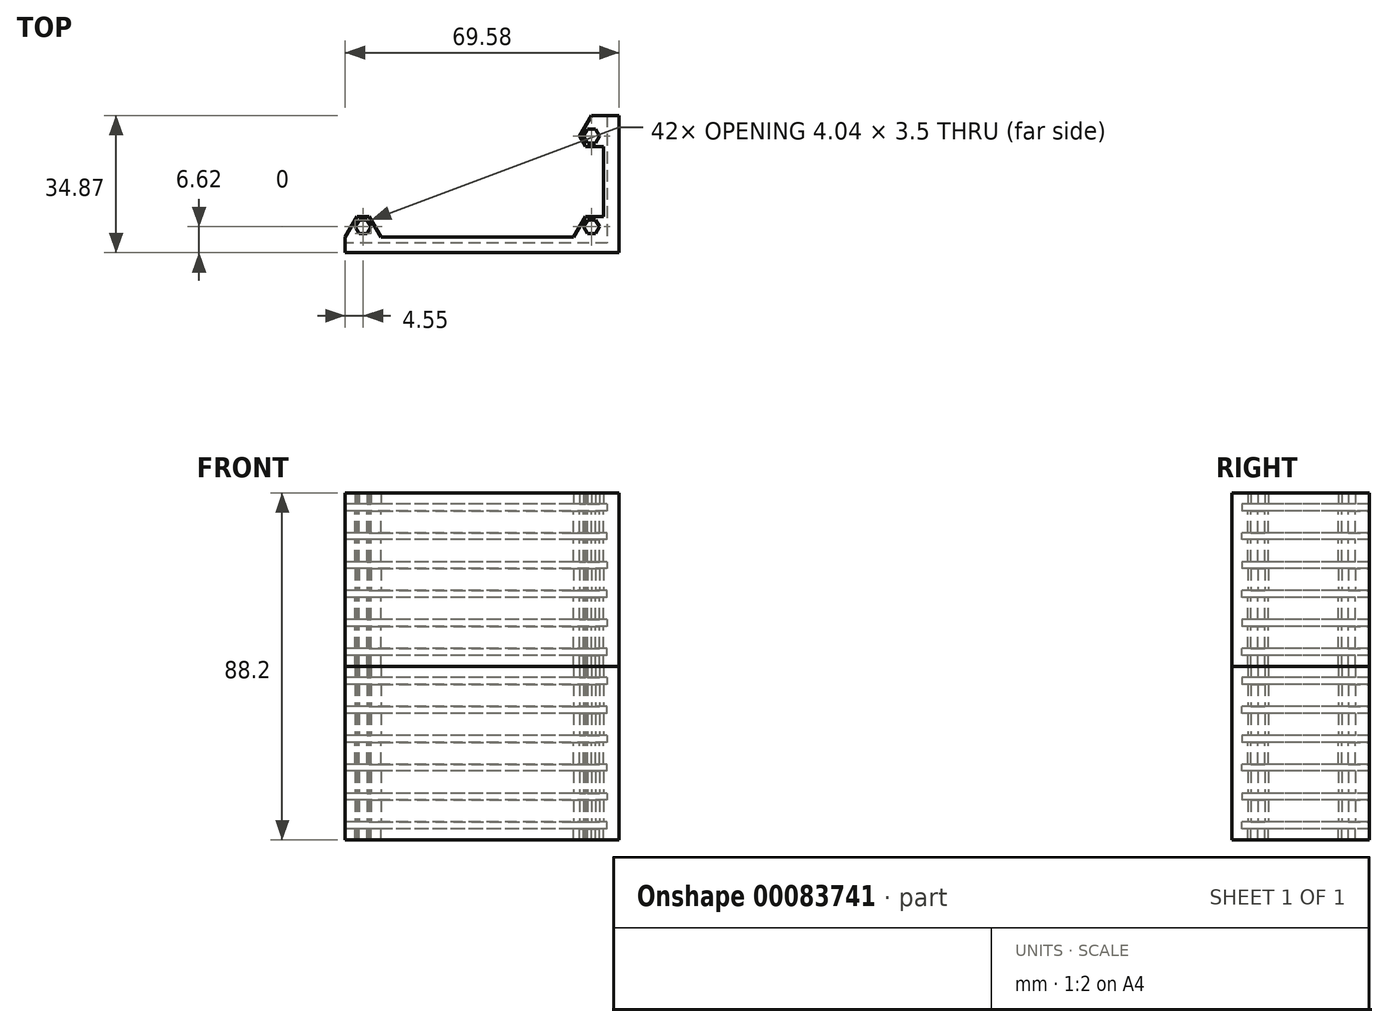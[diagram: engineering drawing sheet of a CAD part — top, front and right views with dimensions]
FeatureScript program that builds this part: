
annotation { "Feature Type Name" : "Feature", "Feature Type Description" : "" }
export const myFeature = defineFeature(function(context is Context, id is Id, definition is map)
    precondition{}
    {
        {
            var Q0;
            Q0=qCreatedBy(makeId("Top.planeOp"),FACE);
            var sketch = newSketch(context, id + "F0", { "sketchPlane" : qUnion([Q0])});
            skLineSegment(sketch, "E0.bottom", {"start": v(-29, 11.5) * mm, "end": v(29, 11.5) * mm, "construction": true});
            skLineSegment(sketch, "E0.top", {"start": v(-29, -11.5) * mm, "end": v(29, -11.5) * mm, "construction": true});
            skLineSegment(sketch, "E0.left", {"start": v(-29, 11.5) * mm, "end": v(-29, -11.5) * mm, "construction": true});
            skLineSegment(sketch, "E0.right", {"start": v(29, 11.5) * mm, "end": v(29, -11.5) * mm, "construction": true});
            skLineSegment(sketch, "E1", {"start": v(0, 11.5) * mm, "end": v(0, -11.5) * mm, "construction": true});
            skCircle(sketch, "E2.cCircle", {"center": v(-29, 11.5) * mm, "radius": 2.62 * mm, "construction": true});
            skLineSegment(sketch, "E2.0", {"start": v(-27.48, 14.12) * mm, "end": v(-25.97, 11.5) * mm});
            skLineSegment(sketch, "E2.1", {"start": v(-25.97, 11.5) * mm, "end": v(-27.48, 8.88) * mm});
            skLineSegment(sketch, "E2.2", {"start": v(-27.48, 8.87) * mm, "end": v(-30.52, 8.87) * mm});
            skLineSegment(sketch, "E2.3", {"start": v(-30.52, 8.88) * mm, "end": v(-32.03, 11.5) * mm});
            skLineSegment(sketch, "E2.4", {"start": v(-32.03, 11.5) * mm, "end": v(-30.52, 14.13) * mm});
            skLineSegment(sketch, "E2.5", {"start": v(-30.52, 14.13) * mm, "end": v(-27.48, 14.13) * mm});
            skLineSegment(sketch, "E3", {"start": v(-29, 0) * mm, "end": v(29, 0) * mm, "construction": true});
            skLineSegment(sketch, "E4.MirrorCS", {"start": v(-27.48, -14.12) * mm, "end": v(-25.97, -11.5) * mm});
            skLineSegment(sketch, "E5.MirrorCS", {"start": v(-25.97, -11.5) * mm, "end": v(-27.48, -8.88) * mm});
            skLineSegment(sketch, "E6.MirrorCS", {"start": v(-27.48, -8.87) * mm, "end": v(-30.52, -8.87) * mm});
            skLineSegment(sketch, "E7.MirrorCS", {"start": v(-30.52, -8.88) * mm, "end": v(-32.03, -11.5) * mm});
            skLineSegment(sketch, "E8.MirrorCS", {"start": v(-30.52, -14.12) * mm, "end": v(-27.48, -14.12) * mm});
            skLineSegment(sketch, "E9.MirrorCS", {"start": v(-32.03, -11.5) * mm, "end": v(-30.52, -14.13) * mm});
            skLineSegment(sketch, "E10.MirrorCS", {"start": v(30.52, -8.87) * mm, "end": v(32.03, -11.5) * mm});
            skLineSegment(sketch, "E11.MirrorCS", {"start": v(32.03, -11.5) * mm, "end": v(30.52, -14.12) * mm});
            skLineSegment(sketch, "E12.MirrorCS", {"start": v(30.52, -14.12) * mm, "end": v(27.48, -14.12) * mm});
            skLineSegment(sketch, "E13.MirrorCS", {"start": v(27.48, -14.12) * mm, "end": v(25.97, -11.5) * mm});
            skLineSegment(sketch, "E14.MirrorCS", {"start": v(25.97, -11.5) * mm, "end": v(27.48, -8.87) * mm});
            skLineSegment(sketch, "E15.MirrorCS", {"start": v(27.48, -8.87) * mm, "end": v(30.52, -8.87) * mm});
            skLineSegment(sketch, "E16.MirrorCS", {"start": v(30.52, 8.87) * mm, "end": v(32.03, 11.5) * mm});
            skLineSegment(sketch, "E17.MirrorCS", {"start": v(32.03, 11.5) * mm, "end": v(30.52, 14.12) * mm});
            skLineSegment(sketch, "E18.MirrorCS", {"start": v(30.52, 14.13) * mm, "end": v(27.48, 14.13) * mm});
            skLineSegment(sketch, "E19.MirrorCS", {"start": v(27.48, 8.88) * mm, "end": v(30.52, 8.88) * mm});
            skLineSegment(sketch, "E20.MirrorCS", {"start": v(27.48, 14.12) * mm, "end": v(25.97, 11.5) * mm});
            skLineSegment(sketch, "E21.MirrorCS", {"start": v(25.97, 11.5) * mm, "end": v(27.48, 8.87) * mm});
            skCircle(sketch, "E22.cCircle", {"center": v(-29, 11.5) * mm, "radius": 1.75 * mm, "construction": true});
            skLineSegment(sketch, "E22.0", {"start": v(-30.01, 13.25) * mm, "end": v(-27.99, 13.25) * mm});
            skLineSegment(sketch, "E22.1", {"start": v(-27.99, 13.25) * mm, "end": v(-26.98, 11.5) * mm});
            skLineSegment(sketch, "E22.2", {"start": v(-26.98, 11.5) * mm, "end": v(-27.99, 9.75) * mm});
            skLineSegment(sketch, "E22.3", {"start": v(-27.99, 9.75) * mm, "end": v(-30.01, 9.75) * mm});
            skLineSegment(sketch, "E22.4", {"start": v(-30.01, 9.75) * mm, "end": v(-31.02, 11.5) * mm});
            skLineSegment(sketch, "E22.5", {"start": v(-31.02, 11.5) * mm, "end": v(-30.01, 13.25) * mm});
            skLineSegment(sketch, "E23.MirrorCS", {"start": v(26.98, 11.5) * mm, "end": v(27.99, 9.75) * mm});
            skLineSegment(sketch, "E24.MirrorCS", {"start": v(27.99, 9.75) * mm, "end": v(30.01, 9.75) * mm});
            skLineSegment(sketch, "E25.MirrorCS", {"start": v(30.01, 9.75) * mm, "end": v(31.02, 11.5) * mm});
            skLineSegment(sketch, "E26.MirrorCS", {"start": v(31.02, 11.5) * mm, "end": v(30.01, 13.25) * mm});
            skLineSegment(sketch, "E27.MirrorCS", {"start": v(30.01, 13.25) * mm, "end": v(27.99, 13.25) * mm});
            skLineSegment(sketch, "E28.MirrorCS", {"start": v(27.99, 13.25) * mm, "end": v(26.98, 11.5) * mm});
            skLineSegment(sketch, "E29.MirrorCS", {"start": v(26.98, -11.5) * mm, "end": v(27.99, -9.75) * mm});
            skLineSegment(sketch, "E30.MirrorCS", {"start": v(27.99, -9.75) * mm, "end": v(30.01, -9.75) * mm});
            skLineSegment(sketch, "E31.MirrorCS", {"start": v(30.01, -9.75) * mm, "end": v(31.02, -11.5) * mm});
            skLineSegment(sketch, "E32.MirrorCS", {"start": v(31.02, -11.5) * mm, "end": v(30.01, -13.25) * mm});
            skLineSegment(sketch, "E33.MirrorCS", {"start": v(30.01, -13.25) * mm, "end": v(27.99, -13.25) * mm});
            skLineSegment(sketch, "E34.MirrorCS", {"start": v(27.99, -13.25) * mm, "end": v(26.98, -11.5) * mm});
            skLineSegment(sketch, "E35.MirrorCS", {"start": v(-31.02, -11.5) * mm, "end": v(-30.01, -13.25) * mm});
            skLineSegment(sketch, "E36.MirrorCS", {"start": v(-30.01, -9.75) * mm, "end": v(-31.02, -11.5) * mm});
            skLineSegment(sketch, "E37.MirrorCS", {"start": v(-27.99, -9.75) * mm, "end": v(-30.01, -9.75) * mm});
            skLineSegment(sketch, "E38.MirrorCS", {"start": v(-26.98, -11.5) * mm, "end": v(-27.99, -9.75) * mm});
            skLineSegment(sketch, "E39.MirrorCS", {"start": v(-30.01, -13.25) * mm, "end": v(-27.99, -13.25) * mm});
            skLineSegment(sketch, "E40.MirrorCS", {"start": v(-27.99, -13.25) * mm, "end": v(-26.98, -11.5) * mm});
            skLineSegment(sketch, "E41.bottom", {"start": v(-32.5, 15.12) * mm, "end": v(32.5, 15.13) * mm});
            skLineSegment(sketch, "E41.top", {"start": v(-32.5, -15.13) * mm, "end": v(32.5, -15.13) * mm});
            skLineSegment(sketch, "E41.left", {"start": v(-32.5, 15.12) * mm, "end": v(-32.5, -15.13) * mm});
            skLineSegment(sketch, "E41.right", {"start": v(32.5, 15.13) * mm, "end": v(32.5, -15.13) * mm});
            skLineSegment(sketch, "E42", {"start": v(32.5, 15.13) * mm, "end": v(-32.5, -15.13) * mm, "construction": true});
            skPoint(sketch, "E43", {"position": v(0, 0) * mm});
            skSolve(sketch);
        }
        {
            var Q0;
            Q0=qCreatedBy(makeId("Top.planeOp"),FACE);
            var sketch = newSketch(context, id + "F1", { "sketchPlane" : qUnion([Q0])});
            skLineSegment(sketch, "E44.0", {"start": v(-30.52, -8.88) * mm, "end": v(-32.03, -11.5) * mm});
            skLineSegment(sketch, "E44.1", {"start": v(-27.48, -8.87) * mm, "end": v(-30.52, -8.87) * mm});
            skLineSegment(sketch, "E44.2", {"start": v(-25.97, -11.5) * mm, "end": v(-27.48, -8.88) * mm});
            skLineSegment(sketch, "E45.0", {"start": v(25.97, -11.5) * mm, "end": v(27.48, -8.87) * mm});
            skLineSegment(sketch, "E45.1", {"start": v(27.48, -8.87) * mm, "end": v(30.52, -8.87) * mm});
            skLineSegment(sketch, "E46.0", {"start": v(25.97, 11.5) * mm, "end": v(27.48, 8.87) * mm});
            skLineSegment(sketch, "E46.1", {"start": v(27.48, 8.88) * mm, "end": v(30.52, 8.88) * mm});
            skLineSegment(sketch, "E47.0", {"start": v(27.48, 14.12) * mm, "end": v(25.97, 11.5) * mm});
            skLineSegment(sketch, "E48", {"start": v(30.52, 8.88) * mm, "end": v(32.03, 8.88) * mm});
            skLineSegment(sketch, "E49", {"start": v(32.03, 8.88) * mm, "end": v(32.03, -8.87) * mm});
            skLineSegment(sketch, "E50", {"start": v(32.03, -8.87) * mm, "end": v(30.52, -8.87) * mm});
            skLineSegment(sketch, "E51", {"start": v(36.03, 16.75) * mm, "end": v(36.03, -18.12) * mm});
            skLineSegment(sketch, "E52", {"start": v(36.03, -18.12) * mm, "end": v(-33.55, -18.13) * mm});
            skLineSegment(sketch, "E53", {"start": v(32.03, 11.5) * mm, "end": v(32.03, 8.88) * mm, "construction": true});
            skLineSegment(sketch, "E54", {"start": v(-25.97, -11.5) * mm, "end": v(-24.45, -14.12) * mm});
            skLineSegment(sketch, "E55", {"start": v(-24.45, -14.12) * mm, "end": v(24.45, -14.12) * mm});
            skLineSegment(sketch, "E56", {"start": v(24.45, -14.12) * mm, "end": v(25.97, -11.5) * mm});
            skLineSegment(sketch, "E57", {"start": v(-24.45, -14.12) * mm, "end": v(-27.48, -14.12) * mm, "construction": true});
            skLineSegment(sketch, "E58.0", {"start": v(-30.01, -9.75) * mm, "end": v(-31.02, -11.5) * mm});
            skLineSegment(sketch, "E58.1", {"start": v(-31.02, -11.5) * mm, "end": v(-30.01, -13.25) * mm});
            skLineSegment(sketch, "E58.2", {"start": v(-30.01, -13.25) * mm, "end": v(-27.99, -13.25) * mm});
            skLineSegment(sketch, "E58.3", {"start": v(-27.99, -13.25) * mm, "end": v(-26.98, -11.5) * mm});
            skLineSegment(sketch, "E58.4", {"start": v(-26.98, -11.5) * mm, "end": v(-27.99, -9.75) * mm});
            skLineSegment(sketch, "E58.5", {"start": v(-27.99, -9.75) * mm, "end": v(-30.01, -9.75) * mm});
            skLineSegment(sketch, "E59.0", {"start": v(26.98, -11.5) * mm, "end": v(27.99, -9.75) * mm});
            skLineSegment(sketch, "E59.1", {"start": v(27.99, -13.25) * mm, "end": v(26.98, -11.5) * mm});
            skLineSegment(sketch, "E59.2", {"start": v(30.01, -13.25) * mm, "end": v(27.99, -13.25) * mm});
            skLineSegment(sketch, "E59.3", {"start": v(31.02, -11.5) * mm, "end": v(30.01, -13.25) * mm});
            skLineSegment(sketch, "E59.4", {"start": v(30.01, -9.75) * mm, "end": v(31.02, -11.5) * mm});
            skLineSegment(sketch, "E59.5", {"start": v(27.99, -9.75) * mm, "end": v(30.01, -9.75) * mm});
            skLineSegment(sketch, "E59.6", {"start": v(27.99, 9.75) * mm, "end": v(30.01, 9.75) * mm});
            skLineSegment(sketch, "E59.7", {"start": v(26.98, 11.5) * mm, "end": v(27.99, 9.75) * mm});
            skLineSegment(sketch, "E59.8", {"start": v(27.99, 13.25) * mm, "end": v(26.98, 11.5) * mm});
            skLineSegment(sketch, "E59.9", {"start": v(30.01, 13.25) * mm, "end": v(27.99, 13.25) * mm});
            skPoint(sketch, "E59.10", {"position": v(31.02, 11.5) * mm});
            skLineSegment(sketch, "E59.11", {"start": v(30.01, 9.75) * mm, "end": v(31.02, 11.5) * mm});
            skLineSegment(sketch, "E59.12", {"start": v(31.02, 11.5) * mm, "end": v(30.01, 13.25) * mm});
            skLineSegment(sketch, "E60", {"start": v(-32.03, -11.5) * mm, "end": v(-33.55, -14.12) * mm});
            skLineSegment(sketch, "E61", {"start": v(-33.55, -14.13) * mm, "end": v(-33.55, -18.12) * mm});
            skLineSegment(sketch, "E62", {"start": v(27.48, 14.12) * mm, "end": v(29, 16.75) * mm});
            skLineSegment(sketch, "E63", {"start": v(36.03, 16.75) * mm, "end": v(29, 16.75) * mm});
            skSolve(sketch);
        }
        {
            var Q0;
            Q0=qSketchRegion(id+"F1",true);
            extrude(context, id + "F2", {"entities" : qUnion([Q0]), "depth" : 2.8 * mm});
        }
        {
            var Q0;
            Q0=makeQuery(id+"F2.opExtrude","CAP_FACE",FACE,{"disambiguationData":[OSD([sQuery(id+"F1.wireOp",EDGE,"E44.0"),sQuery(id+"F1.wireOp",EDGE,"E44.1"),sQuery(id+"F1.wireOp",EDGE,"E44.2"),sQuery(id+"F1.wireOp",EDGE,"E45.0"),sQuery(id+"F1.wireOp",EDGE,"E45.1"),sQuery(id+"F1.wireOp",EDGE,"E46.0"),sQuery(id+"F1.wireOp",EDGE,"E46.1"),sQuery(id+"F1.wireOp",EDGE,"E47.0"),sQuery(id+"F1.wireOp",EDGE,"E48"),sQuery(id+"F1.wireOp",EDGE,"E49"),sQuery(id+"F1.wireOp",EDGE,"E50"),sQuery(id+"F1.wireOp",EDGE,"E51"),sQuery(id+"F1.wireOp",EDGE,"E52"),sQuery(id+"F1.wireOp",EDGE,"E54"),sQuery(id+"F1.wireOp",EDGE,"E55"),sQuery(id+"F1.wireOp",EDGE,"E56"),sQuery(id+"F1.wireOp",EDGE,"E58.0"),sQuery(id+"F1.wireOp",EDGE,"E58.1"),sQuery(id+"F1.wireOp",EDGE,"E58.2"),sQuery(id+"F1.wireOp",EDGE,"E58.3"),sQuery(id+"F1.wireOp",EDGE,"E58.4"),sQuery(id+"F1.wireOp",EDGE,"E58.5"),sQuery(id+"F1.wireOp",EDGE,"E59.0"),sQuery(id+"F1.wireOp",EDGE,"E59.1"),sQuery(id+"F1.wireOp",EDGE,"E59.2"),sQuery(id+"F1.wireOp",EDGE,"E59.3"),sQuery(id+"F1.wireOp",EDGE,"E59.4"),sQuery(id+"F1.wireOp",EDGE,"E59.5"),sQuery(id+"F1.wireOp",EDGE,"E59.6"),sQuery(id+"F1.wireOp",EDGE,"E59.7"),sQuery(id+"F1.wireOp",EDGE,"E59.8"),sQuery(id+"F1.wireOp",EDGE,"E59.9"),sQuery(id+"F1.wireOp",EDGE,"E59.11"),sQuery(id+"F1.wireOp",EDGE,"E59.12"),sQuery(id+"F1.wireOp",EDGE,"E60"),sQuery(id+"F1.wireOp",EDGE,"E61"),sQuery(id+"F1.wireOp",EDGE,"E62"),sQuery(id+"F1.wireOp",EDGE,"E63")])],"isStart":true});
            var sketch = newSketch(context, id + "F3", { "sketchPlane" : qUnion([Q0])});
            skLineSegment(sketch, "E64", {"start": v(-33.55, 18.12) * mm, "end": v(36.03, 18.12) * mm});
            skLineSegment(sketch, "E65", {"start": v(36.03, 18.12) * mm, "end": v(36.03, -16.75) * mm});
            skLineSegment(sketch, "E66", {"start": v(36.03, -16.75) * mm, "end": v(33, -16.75) * mm});
            skLineSegment(sketch, "E67", {"start": v(33, -16.75) * mm, "end": v(33, 15.63) * mm});
            skLineSegment(sketch, "E68", {"start": v(33, 15.63) * mm, "end": v(-33.55, 15.62) * mm});
            skLineSegment(sketch, "E69", {"start": v(-33.55, 15.62) * mm, "end": v(-33.55, 18.12) * mm});
            skSolve(sketch);
        }
        {
            var Q0;
            Q0=qSketchRegion(id+"F3",true);
            extrude(context, id + "F4", {"entities" : qUnion([Q0]), "operationType" : NewBodyOperationType.ADD, "depth" : 1.75 * mm});
        }
        {
            var Q0;
            Q0=makeQuery(id+"F4.opExtrude","CAP_FACE",FACE,{"disambiguationData":[OSD([sQuery(id+"F3.wireOp",EDGE,"E64"),sQuery(id+"F3.wireOp",EDGE,"E65"),sQuery(id+"F3.wireOp",EDGE,"E66"),sQuery(id+"F3.wireOp",EDGE,"E67"),sQuery(id+"F3.wireOp",EDGE,"E68"),sQuery(id+"F3.wireOp",EDGE,"E69")])],"isStart":false});
            var sketch = newSketch(context, id + "F5", { "sketchPlane" : qUnion([Q0])});
            skLineSegment(sketch, "E70.0.0", {"start": v(-27.48, 8.87) * mm, "end": v(-30.52, 8.87) * mm});
            skLineSegment(sketch, "E70.0.1", {"start": v(-30.52, 8.88) * mm, "end": v(-33.55, 14.12) * mm});
            skLineSegment(sketch, "E70.0.2", {"start": v(-33.55, 14.13) * mm, "end": v(-33.55, 18.12) * mm});
            skLineSegment(sketch, "E70.0.3", {"start": v(-33.55, 18.13) * mm, "end": v(36.03, 18.12) * mm});
            skLineSegment(sketch, "E70.0.4", {"start": v(36.03, 18.12) * mm, "end": v(36.03, -16.75) * mm});
            skLineSegment(sketch, "E70.0.5", {"start": v(36.03, -16.75) * mm, "end": v(29, -16.75) * mm});
            skLineSegment(sketch, "E70.0.6", {"start": v(29, -16.75) * mm, "end": v(25.97, -11.5) * mm});
            skLineSegment(sketch, "E70.0.7", {"start": v(25.97, -11.5) * mm, "end": v(27.48, -8.88) * mm});
            skLineSegment(sketch, "E70.0.8", {"start": v(27.48, -8.88) * mm, "end": v(32.03, -8.88) * mm});
            skLineSegment(sketch, "E70.0.9", {"start": v(32.03, -8.88) * mm, "end": v(32.03, 8.87) * mm});
            skLineSegment(sketch, "E70.0.10", {"start": v(32.03, 8.87) * mm, "end": v(27.48, 8.87) * mm});
            skLineSegment(sketch, "E70.0.11", {"start": v(27.48, 8.87) * mm, "end": v(24.45, 14.12) * mm});
            skLineSegment(sketch, "E70.0.12", {"start": v(24.45, 14.12) * mm, "end": v(-24.45, 14.12) * mm});
            skLineSegment(sketch, "E70.0.13", {"start": v(-24.45, 14.12) * mm, "end": v(-27.48, 8.87) * mm});
            skLineSegment(sketch, "E71.0", {"start": v(-30.01, 9.75) * mm, "end": v(-31.02, 11.5) * mm});
            skLineSegment(sketch, "E71.1", {"start": v(-31.02, 11.5) * mm, "end": v(-30.01, 13.25) * mm});
            skLineSegment(sketch, "E71.2", {"start": v(-30.01, 13.25) * mm, "end": v(-27.99, 13.25) * mm});
            skLineSegment(sketch, "E71.3", {"start": v(-27.99, 13.25) * mm, "end": v(-26.98, 11.5) * mm});
            skLineSegment(sketch, "E71.4", {"start": v(-26.98, 11.5) * mm, "end": v(-27.99, 9.75) * mm});
            skLineSegment(sketch, "E71.5", {"start": v(-27.99, 9.75) * mm, "end": v(-30.01, 9.75) * mm});
            skLineSegment(sketch, "E71.6", {"start": v(27.99, 13.25) * mm, "end": v(26.98, 11.5) * mm});
            skLineSegment(sketch, "E71.7", {"start": v(26.98, 11.5) * mm, "end": v(27.99, 9.75) * mm});
            skLineSegment(sketch, "E71.8", {"start": v(27.99, 9.75) * mm, "end": v(30.01, 9.75) * mm});
            skLineSegment(sketch, "E71.9", {"start": v(30.01, 9.75) * mm, "end": v(31.02, 11.5) * mm});
            skLineSegment(sketch, "E71.10", {"start": v(31.02, 11.5) * mm, "end": v(30.01, 13.25) * mm});
            skLineSegment(sketch, "E71.11", {"start": v(30.01, 13.25) * mm, "end": v(27.99, 13.25) * mm});
            skLineSegment(sketch, "E71.12", {"start": v(26.98, -11.5) * mm, "end": v(27.99, -9.75) * mm});
            skLineSegment(sketch, "E71.13", {"start": v(27.99, -13.25) * mm, "end": v(26.98, -11.5) * mm});
            skLineSegment(sketch, "E71.14", {"start": v(30.01, -13.25) * mm, "end": v(27.99, -13.25) * mm});
            skLineSegment(sketch, "E71.15", {"start": v(31.02, -11.5) * mm, "end": v(30.01, -13.25) * mm});
            skLineSegment(sketch, "E71.16", {"start": v(30.01, -9.75) * mm, "end": v(31.02, -11.5) * mm});
            skLineSegment(sketch, "E71.17", {"start": v(27.99, -9.75) * mm, "end": v(30.01, -9.75) * mm});
            skSolve(sketch);
        }
        {
            var Q0;
            Q0=qSketchRegion(id+"F5",true);
            extrude(context, id + "F6", {"entities" : qUnion([Q0]), "operationType" : NewBodyOperationType.ADD, "depth" : 2.8 * mm});
        }
        {
            var Q0;
            Q0=makeQuery(id+"F2.opExtrude","SWEPT_BODY",BODY,{"disambiguationData":[OSD([sQuery(id+"F1.wireOp",EDGE,"E44.0"),sQuery(id+"F1.wireOp",EDGE,"E44.1"),sQuery(id+"F1.wireOp",EDGE,"E44.2"),sQuery(id+"F1.wireOp",EDGE,"E45.0"),sQuery(id+"F1.wireOp",EDGE,"E45.1"),sQuery(id+"F1.wireOp",EDGE,"E46.0"),sQuery(id+"F1.wireOp",EDGE,"E46.1"),sQuery(id+"F1.wireOp",EDGE,"E47.0"),sQuery(id+"F1.wireOp",EDGE,"E48"),sQuery(id+"F1.wireOp",EDGE,"E49"),sQuery(id+"F1.wireOp",EDGE,"E50"),sQuery(id+"F1.wireOp",EDGE,"E51"),sQuery(id+"F1.wireOp",EDGE,"E52"),sQuery(id+"F1.wireOp",EDGE,"E54"),sQuery(id+"F1.wireOp",EDGE,"E55"),sQuery(id+"F1.wireOp",EDGE,"E56"),sQuery(id+"F1.wireOp",EDGE,"E58.0"),sQuery(id+"F1.wireOp",EDGE,"E58.1"),sQuery(id+"F1.wireOp",EDGE,"E58.2"),sQuery(id+"F1.wireOp",EDGE,"E58.3"),sQuery(id+"F1.wireOp",EDGE,"E58.4"),sQuery(id+"F1.wireOp",EDGE,"E58.5"),sQuery(id+"F1.wireOp",EDGE,"E59.0"),sQuery(id+"F1.wireOp",EDGE,"E59.1"),sQuery(id+"F1.wireOp",EDGE,"E59.2"),sQuery(id+"F1.wireOp",EDGE,"E59.3"),sQuery(id+"F1.wireOp",EDGE,"E59.4"),sQuery(id+"F1.wireOp",EDGE,"E59.5"),sQuery(id+"F1.wireOp",EDGE,"E59.6"),sQuery(id+"F1.wireOp",EDGE,"E59.7"),sQuery(id+"F1.wireOp",EDGE,"E59.8"),sQuery(id+"F1.wireOp",EDGE,"E59.9"),sQuery(id+"F1.wireOp",EDGE,"E59.11"),sQuery(id+"F1.wireOp",EDGE,"E59.12"),sQuery(id+"F1.wireOp",EDGE,"E60"),sQuery(id+"F1.wireOp",EDGE,"E61"),sQuery(id+"F1.wireOp",EDGE,"E62"),sQuery(id+"F1.wireOp",EDGE,"E63")])]});
            var Q1;
            Q1=makeQuery(id+"F2.opExtrude","CAP_FACE",FACE,{"disambiguationData":[OSD([sQuery(id+"F1.wireOp",EDGE,"E44.0"),sQuery(id+"F1.wireOp",EDGE,"E44.1"),sQuery(id+"F1.wireOp",EDGE,"E44.2"),sQuery(id+"F1.wireOp",EDGE,"E45.0"),sQuery(id+"F1.wireOp",EDGE,"E45.1"),sQuery(id+"F1.wireOp",EDGE,"E46.0"),sQuery(id+"F1.wireOp",EDGE,"E46.1"),sQuery(id+"F1.wireOp",EDGE,"E47.0"),sQuery(id+"F1.wireOp",EDGE,"E48"),sQuery(id+"F1.wireOp",EDGE,"E49"),sQuery(id+"F1.wireOp",EDGE,"E50"),sQuery(id+"F1.wireOp",EDGE,"E51"),sQuery(id+"F1.wireOp",EDGE,"E52"),sQuery(id+"F1.wireOp",EDGE,"E54"),sQuery(id+"F1.wireOp",EDGE,"E55"),sQuery(id+"F1.wireOp",EDGE,"E56"),sQuery(id+"F1.wireOp",EDGE,"E58.0"),sQuery(id+"F1.wireOp",EDGE,"E58.1"),sQuery(id+"F1.wireOp",EDGE,"E58.2"),sQuery(id+"F1.wireOp",EDGE,"E58.3"),sQuery(id+"F1.wireOp",EDGE,"E58.4"),sQuery(id+"F1.wireOp",EDGE,"E58.5"),sQuery(id+"F1.wireOp",EDGE,"E59.0"),sQuery(id+"F1.wireOp",EDGE,"E59.1"),sQuery(id+"F1.wireOp",EDGE,"E59.2"),sQuery(id+"F1.wireOp",EDGE,"E59.3"),sQuery(id+"F1.wireOp",EDGE,"E59.4"),sQuery(id+"F1.wireOp",EDGE,"E59.5"),sQuery(id+"F1.wireOp",EDGE,"E59.6"),sQuery(id+"F1.wireOp",EDGE,"E59.7"),sQuery(id+"F1.wireOp",EDGE,"E59.8"),sQuery(id+"F1.wireOp",EDGE,"E59.9"),sQuery(id+"F1.wireOp",EDGE,"E59.11"),sQuery(id+"F1.wireOp",EDGE,"E59.12"),sQuery(id+"F1.wireOp",EDGE,"E60"),sQuery(id+"F1.wireOp",EDGE,"E61"),sQuery(id+"F1.wireOp",EDGE,"E62"),sQuery(id+"F1.wireOp",EDGE,"E63")])],"isStart":false});
            mirror(context, id + "F7", {"operationType" : NewBodyOperationType.ADD, "entities" : qUnion([Q0]), "mirrorPlane" : qUnion([Q1])});
        }
        {
            var Q0;
            Q0=makeQuery(id+"F2.opExtrude","SWEPT_BODY",BODY,{"disambiguationData":[OSD([sQuery(id+"F1.wireOp",EDGE,"E44.0"),sQuery(id+"F1.wireOp",EDGE,"E44.1"),sQuery(id+"F1.wireOp",EDGE,"E44.2"),sQuery(id+"F1.wireOp",EDGE,"E45.0"),sQuery(id+"F1.wireOp",EDGE,"E45.1"),sQuery(id+"F1.wireOp",EDGE,"E46.0"),sQuery(id+"F1.wireOp",EDGE,"E46.1"),sQuery(id+"F1.wireOp",EDGE,"E47.0"),sQuery(id+"F1.wireOp",EDGE,"E48"),sQuery(id+"F1.wireOp",EDGE,"E49"),sQuery(id+"F1.wireOp",EDGE,"E50"),sQuery(id+"F1.wireOp",EDGE,"E51"),sQuery(id+"F1.wireOp",EDGE,"E52"),sQuery(id+"F1.wireOp",EDGE,"E54"),sQuery(id+"F1.wireOp",EDGE,"E55"),sQuery(id+"F1.wireOp",EDGE,"E56"),sQuery(id+"F1.wireOp",EDGE,"E58.0"),sQuery(id+"F1.wireOp",EDGE,"E58.1"),sQuery(id+"F1.wireOp",EDGE,"E58.2"),sQuery(id+"F1.wireOp",EDGE,"E58.3"),sQuery(id+"F1.wireOp",EDGE,"E58.4"),sQuery(id+"F1.wireOp",EDGE,"E58.5"),sQuery(id+"F1.wireOp",EDGE,"E59.0"),sQuery(id+"F1.wireOp",EDGE,"E59.1"),sQuery(id+"F1.wireOp",EDGE,"E59.2"),sQuery(id+"F1.wireOp",EDGE,"E59.3"),sQuery(id+"F1.wireOp",EDGE,"E59.4"),sQuery(id+"F1.wireOp",EDGE,"E59.5"),sQuery(id+"F1.wireOp",EDGE,"E59.6"),sQuery(id+"F1.wireOp",EDGE,"E59.7"),sQuery(id+"F1.wireOp",EDGE,"E59.8"),sQuery(id+"F1.wireOp",EDGE,"E59.9"),sQuery(id+"F1.wireOp",EDGE,"E59.11"),sQuery(id+"F1.wireOp",EDGE,"E59.12"),sQuery(id+"F1.wireOp",EDGE,"E60"),sQuery(id+"F1.wireOp",EDGE,"E61"),sQuery(id+"F1.wireOp",EDGE,"E62"),sQuery(id+"F1.wireOp",EDGE,"E63")])]});
            var Q1;
            Q1=makeQuery(id+"F7.opPattern","COPY",FACE,{"derivedFrom":makeQuery(id+"F6.opExtrude","CAP_FACE",FACE,{"disambiguationData":[OSD([sQuery(id+"F5.wireOp",EDGE,"E70.0.0"),sQuery(id+"F5.wireOp",EDGE,"E70.0.1"),sQuery(id+"F5.wireOp",EDGE,"E70.0.2"),sQuery(id+"F5.wireOp",EDGE,"E70.0.3"),sQuery(id+"F5.wireOp",EDGE,"E70.0.4"),sQuery(id+"F5.wireOp",EDGE,"E70.0.5"),sQuery(id+"F5.wireOp",EDGE,"E70.0.6"),sQuery(id+"F5.wireOp",EDGE,"E70.0.7"),sQuery(id+"F5.wireOp",EDGE,"E70.0.8"),sQuery(id+"F5.wireOp",EDGE,"E70.0.9"),sQuery(id+"F5.wireOp",EDGE,"E70.0.10"),sQuery(id+"F5.wireOp",EDGE,"E70.0.11"),sQuery(id+"F5.wireOp",EDGE,"E70.0.12"),sQuery(id+"F5.wireOp",EDGE,"E70.0.13"),sQuery(id+"F5.wireOp",EDGE,"E71.0"),sQuery(id+"F5.wireOp",EDGE,"E71.1"),sQuery(id+"F5.wireOp",EDGE,"E71.2"),sQuery(id+"F5.wireOp",EDGE,"E71.3"),sQuery(id+"F5.wireOp",EDGE,"E71.4"),sQuery(id+"F5.wireOp",EDGE,"E71.5"),sQuery(id+"F5.wireOp",EDGE,"E71.6"),sQuery(id+"F5.wireOp",EDGE,"E71.7"),sQuery(id+"F5.wireOp",EDGE,"E71.8"),sQuery(id+"F5.wireOp",EDGE,"E71.9"),sQuery(id+"F5.wireOp",EDGE,"E71.10"),sQuery(id+"F5.wireOp",EDGE,"E71.11"),sQuery(id+"F5.wireOp",EDGE,"E71.12"),sQuery(id+"F5.wireOp",EDGE,"E71.13"),sQuery(id+"F5.wireOp",EDGE,"E71.14"),sQuery(id+"F5.wireOp",EDGE,"E71.15"),sQuery(id+"F5.wireOp",EDGE,"E71.16"),sQuery(id+"F5.wireOp",EDGE,"E71.17")])],"isStart":false}),"instanceName":"1"});
            mirror(context, id + "F8", {"entities" : qUnion([Q0]), "mirrorPlane" : qUnion([Q1])});
        }
        {
            var Q0;
            Q0=makeQuery(id+"F8.opPattern","COPY",BODY,{"derivedFrom":makeQuery(id+"F2.opExtrude","SWEPT_BODY",BODY,{"disambiguationData":[OSD([sQuery(id+"F1.wireOp",EDGE,"E44.0"),sQuery(id+"F1.wireOp",EDGE,"E44.1"),sQuery(id+"F1.wireOp",EDGE,"E44.2"),sQuery(id+"F1.wireOp",EDGE,"E45.0"),sQuery(id+"F1.wireOp",EDGE,"E45.1"),sQuery(id+"F1.wireOp",EDGE,"E46.0"),sQuery(id+"F1.wireOp",EDGE,"E46.1"),sQuery(id+"F1.wireOp",EDGE,"E47.0"),sQuery(id+"F1.wireOp",EDGE,"E48"),sQuery(id+"F1.wireOp",EDGE,"E49"),sQuery(id+"F1.wireOp",EDGE,"E50"),sQuery(id+"F1.wireOp",EDGE,"E51"),sQuery(id+"F1.wireOp",EDGE,"E52"),sQuery(id+"F1.wireOp",EDGE,"E54"),sQuery(id+"F1.wireOp",EDGE,"E55"),sQuery(id+"F1.wireOp",EDGE,"E56"),sQuery(id+"F1.wireOp",EDGE,"E58.0"),sQuery(id+"F1.wireOp",EDGE,"E58.1"),sQuery(id+"F1.wireOp",EDGE,"E58.2"),sQuery(id+"F1.wireOp",EDGE,"E58.3"),sQuery(id+"F1.wireOp",EDGE,"E58.4"),sQuery(id+"F1.wireOp",EDGE,"E58.5"),sQuery(id+"F1.wireOp",EDGE,"E59.0"),sQuery(id+"F1.wireOp",EDGE,"E59.1"),sQuery(id+"F1.wireOp",EDGE,"E59.2"),sQuery(id+"F1.wireOp",EDGE,"E59.3"),sQuery(id+"F1.wireOp",EDGE,"E59.4"),sQuery(id+"F1.wireOp",EDGE,"E59.5"),sQuery(id+"F1.wireOp",EDGE,"E59.6"),sQuery(id+"F1.wireOp",EDGE,"E59.7"),sQuery(id+"F1.wireOp",EDGE,"E59.8"),sQuery(id+"F1.wireOp",EDGE,"E59.9"),sQuery(id+"F1.wireOp",EDGE,"E59.11"),sQuery(id+"F1.wireOp",EDGE,"E59.12"),sQuery(id+"F1.wireOp",EDGE,"E60"),sQuery(id+"F1.wireOp",EDGE,"E61"),sQuery(id+"F1.wireOp",EDGE,"E62"),sQuery(id+"F1.wireOp",EDGE,"E63")])]}),"instanceName":"1"});
            var Q1;
            Q1=makeQuery(id+"F8.opPattern","COPY",FACE,{"derivedFrom":makeQuery(id+"F6.opExtrude","CAP_FACE",FACE,{"disambiguationData":[OSD([sQuery(id+"F5.wireOp",EDGE,"E70.0.0"),sQuery(id+"F5.wireOp",EDGE,"E70.0.1"),sQuery(id+"F5.wireOp",EDGE,"E70.0.2"),sQuery(id+"F5.wireOp",EDGE,"E70.0.3"),sQuery(id+"F5.wireOp",EDGE,"E70.0.4"),sQuery(id+"F5.wireOp",EDGE,"E70.0.5"),sQuery(id+"F5.wireOp",EDGE,"E70.0.6"),sQuery(id+"F5.wireOp",EDGE,"E70.0.7"),sQuery(id+"F5.wireOp",EDGE,"E70.0.8"),sQuery(id+"F5.wireOp",EDGE,"E70.0.9"),sQuery(id+"F5.wireOp",EDGE,"E70.0.10"),sQuery(id+"F5.wireOp",EDGE,"E70.0.11"),sQuery(id+"F5.wireOp",EDGE,"E70.0.12"),sQuery(id+"F5.wireOp",EDGE,"E70.0.13"),sQuery(id+"F5.wireOp",EDGE,"E71.0"),sQuery(id+"F5.wireOp",EDGE,"E71.1"),sQuery(id+"F5.wireOp",EDGE,"E71.2"),sQuery(id+"F5.wireOp",EDGE,"E71.3"),sQuery(id+"F5.wireOp",EDGE,"E71.4"),sQuery(id+"F5.wireOp",EDGE,"E71.5"),sQuery(id+"F5.wireOp",EDGE,"E71.6"),sQuery(id+"F5.wireOp",EDGE,"E71.7"),sQuery(id+"F5.wireOp",EDGE,"E71.8"),sQuery(id+"F5.wireOp",EDGE,"E71.9"),sQuery(id+"F5.wireOp",EDGE,"E71.10"),sQuery(id+"F5.wireOp",EDGE,"E71.11"),sQuery(id+"F5.wireOp",EDGE,"E71.12"),sQuery(id+"F5.wireOp",EDGE,"E71.13"),sQuery(id+"F5.wireOp",EDGE,"E71.14"),sQuery(id+"F5.wireOp",EDGE,"E71.15"),sQuery(id+"F5.wireOp",EDGE,"E71.16"),sQuery(id+"F5.wireOp",EDGE,"E71.17")])],"isStart":false}),"instanceName":"1"});
            mirror(context, id + "F9", {"operationType" : NewBodyOperationType.ADD, "entities" : qUnion([Q0]), "mirrorPlane" : qUnion([Q1])});
        }
        {
            var Q0;
            Q0=makeQuery(id+"F8.opPattern","COPY",BODY,{"derivedFrom":makeQuery(id+"F2.opExtrude","SWEPT_BODY",BODY,{"disambiguationData":[OSD([sQuery(id+"F1.wireOp",EDGE,"E44.0"),sQuery(id+"F1.wireOp",EDGE,"E44.1"),sQuery(id+"F1.wireOp",EDGE,"E44.2"),sQuery(id+"F1.wireOp",EDGE,"E45.0"),sQuery(id+"F1.wireOp",EDGE,"E45.1"),sQuery(id+"F1.wireOp",EDGE,"E46.0"),sQuery(id+"F1.wireOp",EDGE,"E46.1"),sQuery(id+"F1.wireOp",EDGE,"E47.0"),sQuery(id+"F1.wireOp",EDGE,"E48"),sQuery(id+"F1.wireOp",EDGE,"E49"),sQuery(id+"F1.wireOp",EDGE,"E50"),sQuery(id+"F1.wireOp",EDGE,"E51"),sQuery(id+"F1.wireOp",EDGE,"E52"),sQuery(id+"F1.wireOp",EDGE,"E54"),sQuery(id+"F1.wireOp",EDGE,"E55"),sQuery(id+"F1.wireOp",EDGE,"E56"),sQuery(id+"F1.wireOp",EDGE,"E58.0"),sQuery(id+"F1.wireOp",EDGE,"E58.1"),sQuery(id+"F1.wireOp",EDGE,"E58.2"),sQuery(id+"F1.wireOp",EDGE,"E58.3"),sQuery(id+"F1.wireOp",EDGE,"E58.4"),sQuery(id+"F1.wireOp",EDGE,"E58.5"),sQuery(id+"F1.wireOp",EDGE,"E59.0"),sQuery(id+"F1.wireOp",EDGE,"E59.1"),sQuery(id+"F1.wireOp",EDGE,"E59.2"),sQuery(id+"F1.wireOp",EDGE,"E59.3"),sQuery(id+"F1.wireOp",EDGE,"E59.4"),sQuery(id+"F1.wireOp",EDGE,"E59.5"),sQuery(id+"F1.wireOp",EDGE,"E59.6"),sQuery(id+"F1.wireOp",EDGE,"E59.7"),sQuery(id+"F1.wireOp",EDGE,"E59.8"),sQuery(id+"F1.wireOp",EDGE,"E59.9"),sQuery(id+"F1.wireOp",EDGE,"E59.11"),sQuery(id+"F1.wireOp",EDGE,"E59.12"),sQuery(id+"F1.wireOp",EDGE,"E60"),sQuery(id+"F1.wireOp",EDGE,"E61"),sQuery(id+"F1.wireOp",EDGE,"E62"),sQuery(id+"F1.wireOp",EDGE,"E63")])]}),"instanceName":"1"});
            var Q1;
            Q1=makeQuery(id+"F2.opExtrude","SWEPT_BODY",BODY,{"disambiguationData":[OSD([sQuery(id+"F1.wireOp",EDGE,"E44.0"),sQuery(id+"F1.wireOp",EDGE,"E44.1"),sQuery(id+"F1.wireOp",EDGE,"E44.2"),sQuery(id+"F1.wireOp",EDGE,"E45.0"),sQuery(id+"F1.wireOp",EDGE,"E45.1"),sQuery(id+"F1.wireOp",EDGE,"E46.0"),sQuery(id+"F1.wireOp",EDGE,"E46.1"),sQuery(id+"F1.wireOp",EDGE,"E47.0"),sQuery(id+"F1.wireOp",EDGE,"E48"),sQuery(id+"F1.wireOp",EDGE,"E49"),sQuery(id+"F1.wireOp",EDGE,"E50"),sQuery(id+"F1.wireOp",EDGE,"E51"),sQuery(id+"F1.wireOp",EDGE,"E52"),sQuery(id+"F1.wireOp",EDGE,"E54"),sQuery(id+"F1.wireOp",EDGE,"E55"),sQuery(id+"F1.wireOp",EDGE,"E56"),sQuery(id+"F1.wireOp",EDGE,"E58.0"),sQuery(id+"F1.wireOp",EDGE,"E58.1"),sQuery(id+"F1.wireOp",EDGE,"E58.2"),sQuery(id+"F1.wireOp",EDGE,"E58.3"),sQuery(id+"F1.wireOp",EDGE,"E58.4"),sQuery(id+"F1.wireOp",EDGE,"E58.5"),sQuery(id+"F1.wireOp",EDGE,"E59.0"),sQuery(id+"F1.wireOp",EDGE,"E59.1"),sQuery(id+"F1.wireOp",EDGE,"E59.2"),sQuery(id+"F1.wireOp",EDGE,"E59.3"),sQuery(id+"F1.wireOp",EDGE,"E59.4"),sQuery(id+"F1.wireOp",EDGE,"E59.5"),sQuery(id+"F1.wireOp",EDGE,"E59.6"),sQuery(id+"F1.wireOp",EDGE,"E59.7"),sQuery(id+"F1.wireOp",EDGE,"E59.8"),sQuery(id+"F1.wireOp",EDGE,"E59.9"),sQuery(id+"F1.wireOp",EDGE,"E59.11"),sQuery(id+"F1.wireOp",EDGE,"E59.12"),sQuery(id+"F1.wireOp",EDGE,"E60"),sQuery(id+"F1.wireOp",EDGE,"E61"),sQuery(id+"F1.wireOp",EDGE,"E62"),sQuery(id+"F1.wireOp",EDGE,"E63")])]});
            var Q2;
            Q2=makeQuery(id+"F9.opPattern","COPY",FACE,{"derivedFrom":makeQuery(id+"F8.opPattern","COPY",FACE,{"derivedFrom":makeQuery(id+"F7.opPattern","COPY",FACE,{"derivedFrom":makeQuery(id+"F6.opExtrude","CAP_FACE",FACE,{"disambiguationData":[OSD([sQuery(id+"F5.wireOp",EDGE,"E70.0.0"),sQuery(id+"F5.wireOp",EDGE,"E70.0.1"),sQuery(id+"F5.wireOp",EDGE,"E70.0.2"),sQuery(id+"F5.wireOp",EDGE,"E70.0.3"),sQuery(id+"F5.wireOp",EDGE,"E70.0.4"),sQuery(id+"F5.wireOp",EDGE,"E70.0.5"),sQuery(id+"F5.wireOp",EDGE,"E70.0.6"),sQuery(id+"F5.wireOp",EDGE,"E70.0.7"),sQuery(id+"F5.wireOp",EDGE,"E70.0.8"),sQuery(id+"F5.wireOp",EDGE,"E70.0.9"),sQuery(id+"F5.wireOp",EDGE,"E70.0.10"),sQuery(id+"F5.wireOp",EDGE,"E70.0.11"),sQuery(id+"F5.wireOp",EDGE,"E70.0.12"),sQuery(id+"F5.wireOp",EDGE,"E70.0.13"),sQuery(id+"F5.wireOp",EDGE,"E71.0"),sQuery(id+"F5.wireOp",EDGE,"E71.1"),sQuery(id+"F5.wireOp",EDGE,"E71.2"),sQuery(id+"F5.wireOp",EDGE,"E71.3"),sQuery(id+"F5.wireOp",EDGE,"E71.4"),sQuery(id+"F5.wireOp",EDGE,"E71.5"),sQuery(id+"F5.wireOp",EDGE,"E71.6"),sQuery(id+"F5.wireOp",EDGE,"E71.7"),sQuery(id+"F5.wireOp",EDGE,"E71.8"),sQuery(id+"F5.wireOp",EDGE,"E71.9"),sQuery(id+"F5.wireOp",EDGE,"E71.10"),sQuery(id+"F5.wireOp",EDGE,"E71.11"),sQuery(id+"F5.wireOp",EDGE,"E71.12"),sQuery(id+"F5.wireOp",EDGE,"E71.13"),sQuery(id+"F5.wireOp",EDGE,"E71.14"),sQuery(id+"F5.wireOp",EDGE,"E71.15"),sQuery(id+"F5.wireOp",EDGE,"E71.16"),sQuery(id+"F5.wireOp",EDGE,"E71.17")])],"isStart":false}),"instanceName":"1"}),"instanceName":"1"}),"instanceName":"1"});
            mirror(context, id + "F10", {"entities" : qUnion([Q0, Q1]), "mirrorPlane" : qUnion([Q2])});
        }
    });
